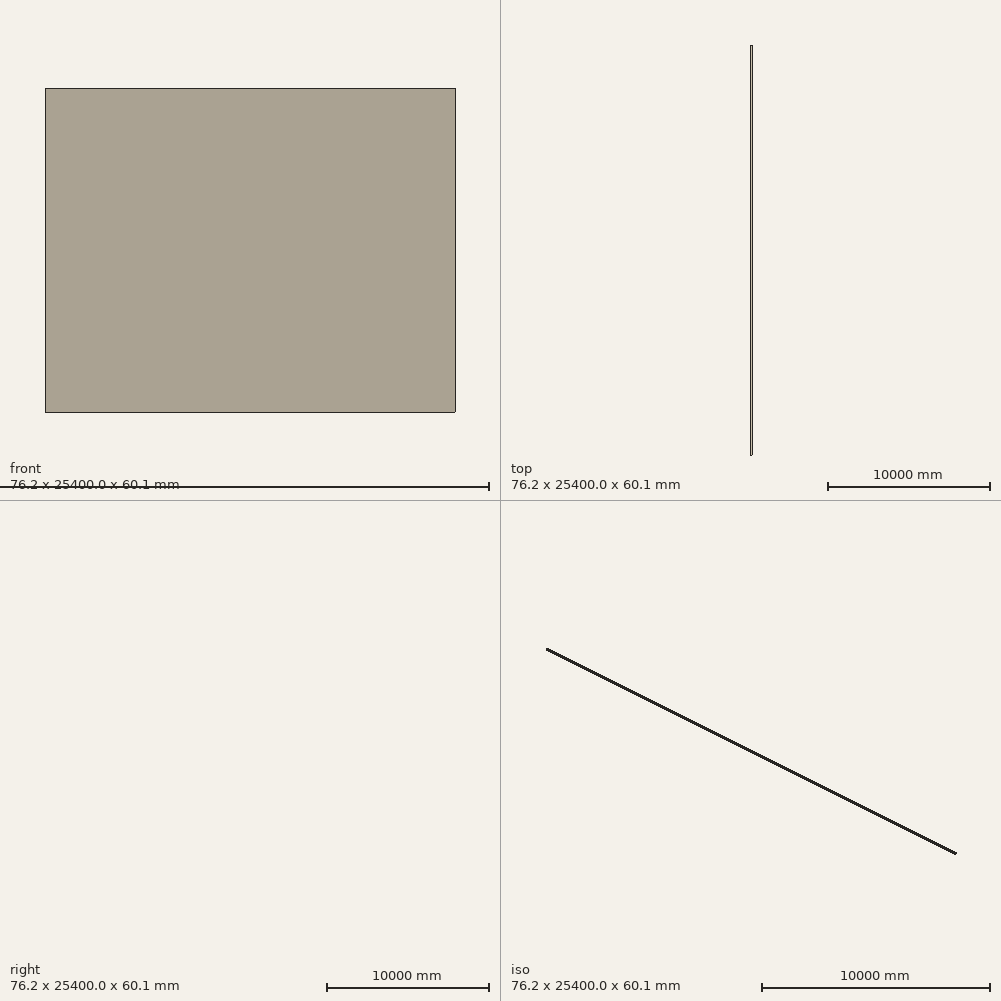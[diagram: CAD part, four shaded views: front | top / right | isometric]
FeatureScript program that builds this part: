
annotation { "Feature Type Name" : "Feature", "Feature Type Description" : "" }
export const myFeature = defineFeature(function(context is Context, id is Id, definition is map)
    precondition{}
    {
        {
            var Q0;
            Q0=qCreatedBy(makeId("Front.planeOp"),FACE);
            var sketch = newSketch(context, id + "F0", { "sketchPlane" : qUnion([Q0])});
            skLineSegment(sketch, "E0.bottom", {"start": v(-38.09, 30.06) * mm, "end": v(38.09, 30.06) * mm});
            skLineSegment(sketch, "E0.top", {"start": v(-38.09, -30.06) * mm, "end": v(38.09, -30.06) * mm});
            skLineSegment(sketch, "E0.left", {"start": v(-38.09, 30.06) * mm, "end": v(-38.09, -30.06) * mm});
            skLineSegment(sketch, "E0.right", {"start": v(38.09, 30.06) * mm, "end": v(38.09, -30.06) * mm});
            skPoint(sketch, "E0.middle", {"position": v(0, 0) * mm});
            skSolve(sketch);
        }
        {
            var Q0;
            Q0=makeQuery(id+"F0.imprint","IMPRINT",FACE,{"disambiguationData":[TD([[makeQuery(id+"F0.imprint","IMPRINT",EDGE,{"derivedFrom":sQuery(id+"F0.wireOp",EDGE,"E0.bottom")}),-1.0]])]});
            extrude(context, id + "F1", {"entities" : qUnion([Q0]), "endBound" : BoundingType.SYMMETRIC, "depth" : 25400 * mm, "offsetDistance" : 25.4 * mm});
        }
    });
